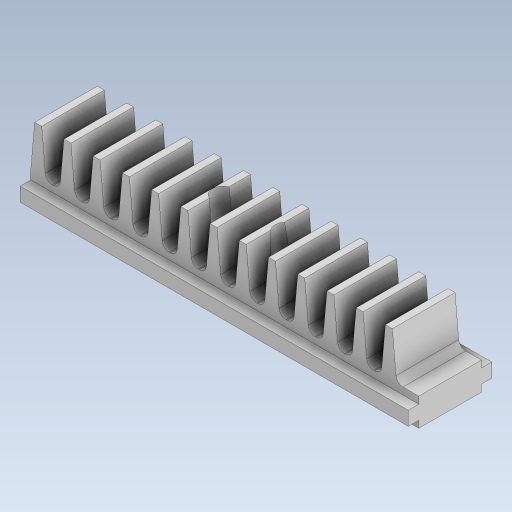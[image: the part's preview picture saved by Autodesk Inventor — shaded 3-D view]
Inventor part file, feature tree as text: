
AUTODESK INVENTOR PART (.ipt)
format: ipt  version: 2023.5 (Build 275446000, 446)  size: 287,232 bytes
history: native  units: in
note: dims shown in document units (in); Inventor stores cm internally (conversion verified against a paired STEP export)
features: extrude x4, sketch x3, fillet x2, pattern_linear x1, plane x1
ambient origin geometry x8: Origin, YZ Plane, XZ Plane, XY Plane, X Axis, Y Axis, Z Axis, Center Point
bodies: Solid1 (feature_tree)
feature tree (11):
  sketch  "Sketch1"  dims[d29=0.1378in d30=0.1181in]
  extrude  "Extrusion1"  Depth=0.1181in
  extrude  "Extrusion2"  Depth=0.0618in
  fillet  "Fillet1"  Radius=0.0309in
  pattern_linear  "Rectangular Pattern1"  Spacing1=0.0866in  [1 undecoded]
  fillet  "Fillet2"  Radius=0.1575in
  plane  "Work Plane1"
  extrude  "Extrusion3"  Depth=0.3543in TaperAngle=0.0deg
  extrude  "Extrusion4"  Depth=0.3543in TaperAngle=0.0deg
  sketch  "Sketch2"  dims[d31=0.1181in d32=0.0618in d33=0.0309in]
  sketch  "Sketch3"  dims[d34=0.0394in d35=0.0866in d36=0.1575in d37=0.3543in d38=0.0in d39=0.3543in d40=0.0in d41=0.0394in d42=5.1181in d44=0.1654in d45=0.0394in d46=0.0787in d47=0.0394in d48=0.4724in d49=0.0in d50=0.1181in d51=0.1181in d52=0.3543in d53=0.4724in d54=0.0in]
note: 1 required parameter value undecoded (feature->parameter linkage not recoverable at this tier; creation-order binding heuristic only, values carry confidence <= 0.55)
